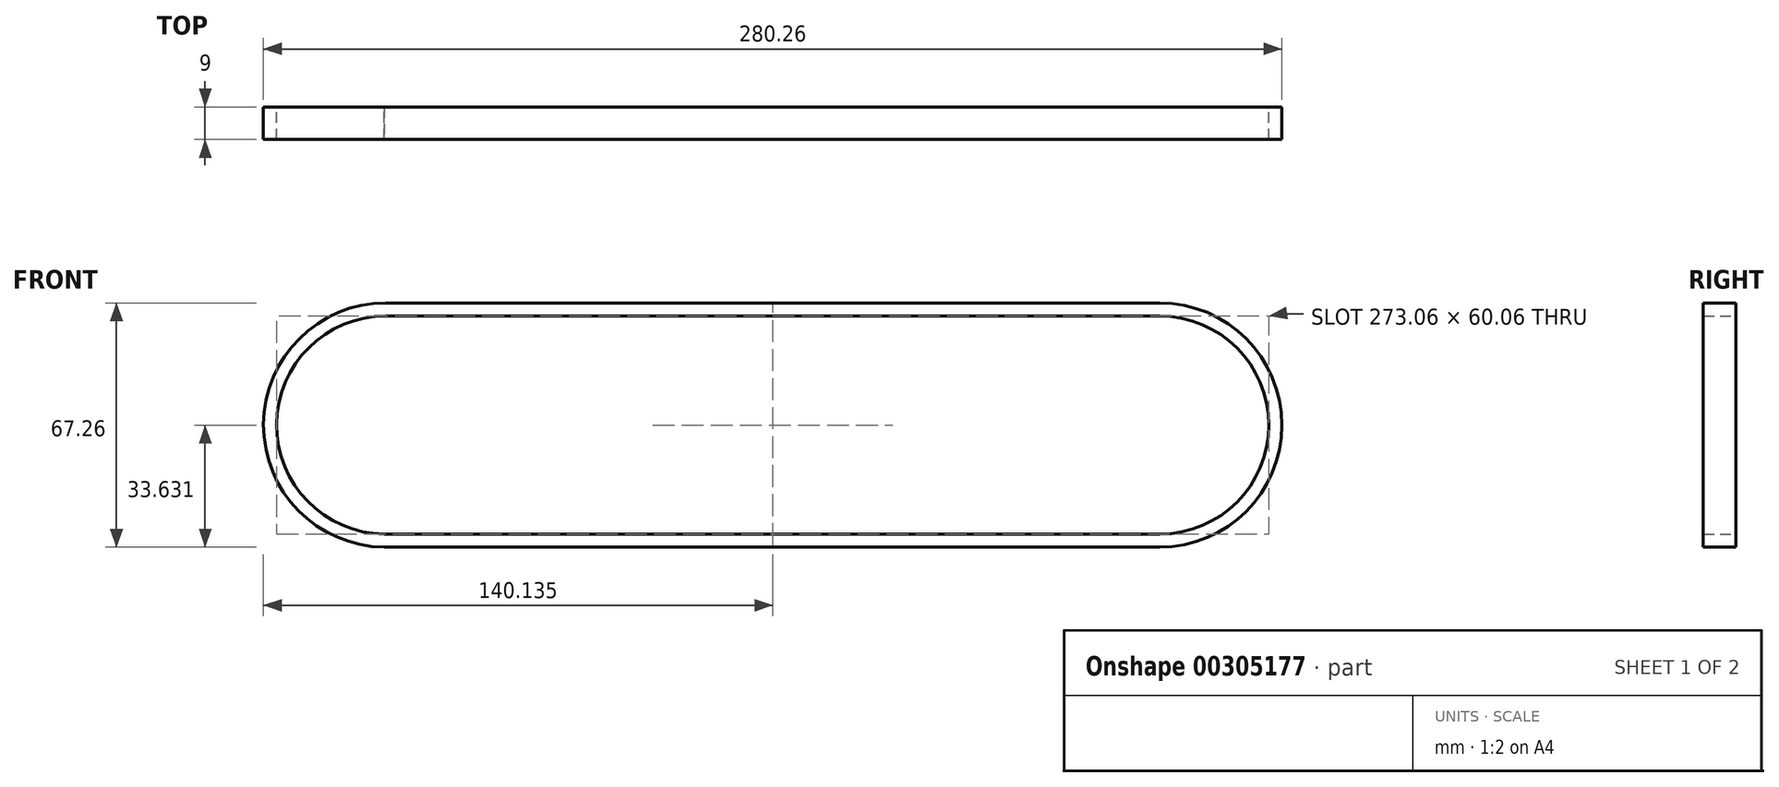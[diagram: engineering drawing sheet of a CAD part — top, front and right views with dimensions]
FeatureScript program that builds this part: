
annotation { "Feature Type Name" : "Feature", "Feature Type Description" : "" }
export const myFeature = defineFeature(function(context is Context, id is Id, definition is map)
    precondition{}
    {
        {
            var Q0;
            Q0=qCreatedBy(makeId("Front.planeOp"),FACE);
            var sketch = newSketch(context, id + "F0", { "sketchPlane" : qUnion([Q0])});
            skLineSegment(sketch, "E0.left", {"start": v(-525.03, 486.56) * mm, "end": v(-525.03, 486.56) * mm});
            skLineSegment(sketch, "E1", {"start": v(64.33, 486.56) * mm, "end": v(64.33, 701.79) * mm, "construction": true});
            skLineSegment(sketch, "E2", {"start": v(-522.39, 458.03) * mm, "end": v(12.71, 507.63) * mm});
            skArc(sketch, "E3", {"start": v(12.71, 507.63) * mm, "mid": v(4.8, 475.52) * mm, "end": v(30.9, 495.85) * mm});
            skArc(sketch, "E4", {"start": v(30.9, 495.85) * mm, "mid": v(23.84, 504.9) * mm, "end": v(12.71, 507.63) * mm});
            skArc(sketch, "E5", {"start": v(97.76, 477.26) * mm, "mid": v(104.86, 468.18) * mm, "end": v(116.06, 465.49) * mm});
            skArc(sketch, "E6", {"start": v(116.06, 465.49) * mm, "mid": v(123.8, 497.62) * mm, "end": v(97.76, 477.26) * mm});
            skArc(sketch, "E7", {"start": v(-525.12, 515.2) * mm, "mid": v(-553.65, 485.2) * mm, "end": v(-522.39, 458.03) * mm});
            skArc(sketch, "E8", {"start": v(-522.39, 458.03) * mm, "mid": v(-496.41, 487.93) * mm, "end": v(-525.12, 515.2) * mm});
            skLineSegment(sketch, "E9", {"start": v(-525.03, 486.56) * mm, "end": v(652.97, 490.2) * mm, "construction": true});
            skPoint(sketch, "E10.startSnap0", {"position": v(104.86, 468.18) * mm});
            skLineSegment(sketch, "E11", {"start": v(64.78, 463.39) * mm, "end": v(653.05, 465.2) * mm});
            skLineSegment(sketch, "E12", {"start": v(652.78, 515.2) * mm, "end": v(116.06, 465.49) * mm});
            skLineSegment(sketch, "E13", {"start": v(64.33, 513.38) * mm, "end": v(-525.12, 515.2) * mm});
            skLineSegment(sketch, "E14", {"start": v(30.9, 495.85) * mm, "end": v(42.8, 475.68) * mm});
            skLineSegment(sketch, "E15", {"start": v(97.76, 477.26) * mm, "end": v(86.72, 499.5) * mm});
            skArc(sketch, "E16", {"start": v(64.33, 513.38) * mm, "mid": v(42.62, 500.78) * mm, "end": v(42.8, 475.68) * mm});
            skArc(sketch, "E17", {"start": v(86.72, 499.5) * mm, "mid": v(77.5, 509.63) * mm, "end": v(64.33, 513.38) * mm});
            skArc(sketch, "E18", {"start": v(652.78, 515.2) * mm, "mid": v(627.97, 490.07) * mm, "end": v(653.05, 465.2) * mm});
            skArc(sketch, "E19", {"start": v(653.05, 465.2) * mm, "mid": v(677.97, 490.34) * mm, "end": v(652.78, 515.2) * mm});
            skArc(sketch, "E20", {"start": v(42.8, 475.68) * mm, "mid": v(52.13, 466.56) * mm, "end": v(64.78, 463.39) * mm});
            skArc(sketch, "E21", {"start": v(64.78, 463.39) * mm, "mid": v(85.7, 475.4) * mm, "end": v(86.72, 499.5) * mm});
            skLineSegment(sketch, "E22", {"start": v(-525.03, 262.8) * mm, "end": v(652.97, 262.8) * mm, "construction": true});
            skLineSegment(sketch, "E23", {"start": v(63.97, 262.8) * mm, "end": v(63.97, 388.17) * mm, "construction": true});
            skLineSegment(sketch, "E24", {"start": v(-525.03, 230.98) * mm, "end": v(1.52, 285.15) * mm});
            skLineSegment(sketch, "E25", {"start": v(-525.03, 294.64) * mm, "end": v(63.97, 294.64) * mm});
            skLineSegment(sketch, "E26", {"start": v(19.1, 276.61) * mm, "end": v(36.47, 246.79) * mm});
            skLineSegment(sketch, "E27", {"start": v(63.97, 230.98) * mm, "end": v(652.97, 230.98) * mm});
            skLineSegment(sketch, "E28", {"start": v(91.47, 278.83) * mm, "end": v(108.85, 249) * mm});
            skLineSegment(sketch, "E29", {"start": v(125.77, 240.4) * mm, "end": v(649.7, 294.47) * mm});
            skArc(sketch, "E30", {"start": v(-525.03, 294.64) * mm, "mid": v(-556.86, 262.8) * mm, "end": v(-525.03, 230.98) * mm});
            skArc(sketch, "E31", {"start": v(-525.03, 230.98) * mm, "mid": v(-493.2, 262.8) * mm, "end": v(-525.03, 294.64) * mm});
            skArc(sketch, "E32", {"start": v(1.36, 285.1) * mm, "mid": v(-3.59, 252.02) * mm, "end": v(19.1, 276.61) * mm});
            skArc(sketch, "E33", {"start": v(19.1, 276.61) * mm, "mid": v(11.53, 283.59) * mm, "end": v(1.36, 285.1) * mm});
            skArc(sketch, "E34", {"start": v(36.47, 246.79) * mm, "mid": v(48.1, 235.21) * mm, "end": v(63.97, 230.98) * mm});
            skArc(sketch, "E35", {"start": v(63.97, 230.98) * mm, "mid": v(91.57, 246.94) * mm, "end": v(91.47, 278.83) * mm});
            skArc(sketch, "E36", {"start": v(63.97, 294.64) * mm, "mid": v(36.37, 278.67) * mm, "end": v(36.47, 246.79) * mm});
            skArc(sketch, "E37", {"start": v(91.47, 278.83) * mm, "mid": v(79.83, 290.4) * mm, "end": v(63.97, 294.64) * mm});
            skArc(sketch, "E38", {"start": v(108.85, 249) * mm, "mid": v(116.04, 242.2) * mm, "end": v(125.77, 240.4) * mm});
            skArc(sketch, "E39", {"start": v(125.77, 240.4) * mm, "mid": v(131.9, 273.4) * mm, "end": v(108.85, 249) * mm});
            skArc(sketch, "E40", {"start": v(649.7, 294.47) * mm, "mid": v(621.18, 261.17) * mm, "end": v(652.97, 230.98) * mm});
            skArc(sketch, "E41", {"start": v(652.97, 230.98) * mm, "mid": v(684.76, 264.44) * mm, "end": v(649.7, 294.47) * mm});
            skCircle(sketch, "E42", {"center": v(652.97, 2.27) * mm, "radius": 31.83 * mm});
            skLineSegment(sketch, "E43", {"start": v(5.35, -6.02) * mm, "end": v(43.27, 26.45) * mm});
            skLineSegment(sketch, "E44", {"start": v(-7.53, -10.16) * mm, "end": v(-522.3, 33.99) * mm});
            skArc(sketch, "E45", {"start": v(-522.3, 33.99) * mm, "mid": v(-556.83, 3.63) * mm, "end": v(-525.03, -29.56) * mm});
            skArc(sketch, "E46", {"start": v(-525.03, -29.56) * mm, "mid": v(-517.68, -28.7) * mm, "end": v(-510.72, -26.16) * mm});
            skArc(sketch, "E47", {"start": v(-7.53, -10.16) * mm, "mid": v(-0.67, -9.39) * mm, "end": v(5.35, -6.02) * mm});
            skArc(sketch, "E48", {"start": v(5.35, -6.02) * mm, "mid": v(-11.4, 23.93) * mm, "end": v(-7.53, -10.16) * mm});
            skArc(sketch, "E49", {"start": v(43.84, 26.93) * mm, "mid": v(33.99, -8.41) * mm, "end": v(63.97, -29.56) * mm});
            skLineSegment(sketch, "E50", {"start": v(63.97, -29.56) * mm, "end": v(63.97, -29.56) * mm});
            skLineSegment(sketch, "E51", {"start": v(-525.03, 2.27) * mm, "end": v(170.78, 2.27) * mm, "construction": true});
            skLineSegment(sketch, "E52", {"start": v(-525.03, 2.27) * mm, "end": v(-525.03, 58.63) * mm, "construction": true});
            skLineSegment(sketch, "E53", {"start": v(63.97, -29.56) * mm, "end": v(-453.54, 14.7) * mm});
            skArc(sketch, "E54", {"start": v(-462.9, 12.9) * mm, "mid": v(-451.72, -19.91) * mm, "end": v(-453.54, 14.7) * mm});
            skArc(sketch, "E55", {"start": v(-453.54, 14.7) * mm, "mid": v(-458.34, 14.46) * mm, "end": v(-462.9, 12.9) * mm});
            skLineSegment(sketch, "E56", {"start": v(-525.03, -29.56) * mm, "end": v(-525.03, -29.56) * mm});
            skArc(sketch, "E57", {"start": v(-510.72, -26.16) * mm, "mid": v(-493.77, 8.3) * mm, "end": v(-522.3, 33.99) * mm});
            skArc(sketch, "E58", {"start": v(43.27, 26.45) * mm, "mid": v(84.39, -22.15) * mm, "end": v(43.84, 26.93) * mm});
            skArc(sketch, "E59", {"start": v(63.97, -29.56) * mm, "mid": v(93.83, 13.3) * mm, "end": v(43.27, 26.45) * mm});
            skLineSegment(sketch, "E60", {"start": v(-504.33, -21.9) * mm, "end": v(-466.41, 10.56) * mm});
            skLineSegment(sketch, "E61", {"start": v(-504.33, -244.07) * mm, "end": v(154.7, -244.07) * mm, "construction": true});
            skLineSegment(sketch, "E62", {"start": v(60.46, -282.1) * mm, "end": v(-432.72, -236.64) * mm});
            skLineSegment(sketch, "E63", {"start": v(-446.45, -241.44) * mm, "end": v(-446.6, -241.6) * mm});
            skLineSegment(sketch, "E64", {"start": v(-500.82, -206.03) * mm, "end": v(-7.64, -251.5) * mm});
            skLineSegment(sketch, "E65", {"start": v(6.1, -246.69) * mm, "end": v(37.5, -216.51) * mm});
            skArc(sketch, "E66", {"start": v(37.5, -216.51) * mm, "mid": v(27.91, -256.68) * mm, "end": v(60.46, -282.1) * mm});
            skArc(sketch, "E67", {"start": v(60.46, -282.1) * mm, "mid": v(100.03, -231.45) * mm, "end": v(37.5, -216.51) * mm});
            skArc(sketch, "E68", {"start": v(6.1, -246.69) * mm, "mid": v(-11.81, -217.55) * mm, "end": v(-7.64, -251.5) * mm});
            skArc(sketch, "E69", {"start": v(-7.64, -251.5) * mm, "mid": v(-0.25, -250.58) * mm, "end": v(6.1, -246.69) * mm});
            skLineSegment(sketch, "E70", {"start": v(-446.6, -241.6) * mm, "end": v(-477.87, -271.62) * mm});
            skArc(sketch, "E71", {"start": v(-446.45, -241.44) * mm, "mid": v(-428.55, -270.58) * mm, "end": v(-432.72, -236.64) * mm});
            skArc(sketch, "E72", {"start": v(-432.72, -236.64) * mm, "mid": v(-440.1, -237.55) * mm, "end": v(-446.45, -241.44) * mm});
            skArc(sketch, "E73", {"start": v(-477.87, -271.62) * mm, "mid": v(-468.27, -231.45) * mm, "end": v(-500.82, -206.03) * mm});
            skArc(sketch, "E74", {"start": v(-500.82, -206.03) * mm, "mid": v(-540.38, -256.68) * mm, "end": v(-477.87, -271.62) * mm});
            skLineSegment(sketch, "E75", {"start": v(-504.33, -545.9) * mm, "end": v(460.67, -545.9) * mm, "construction": true});
            skPoint(sketch, "E76.centerSnap0", {"position": v(-21.83, -545.9) * mm});
            skLineSegment(sketch, "E77", {"start": v(-504.33, -514.08) * mm, "end": v(460.67, -514.08) * mm});
            skLineSegment(sketch, "E78", {"start": v(460.28, -577.74) * mm, "end": v(-383.7, -544.92) * mm});
            skLineSegment(sketch, "E79", {"start": v(-495.46, -576.48) * mm, "end": v(-388.78, -545.54) * mm});
            skArc(sketch, "E80", {"start": v(-388.78, -545.54) * mm, "mid": v(-382.38, -576.8) * mm, "end": v(-383.7, -544.92) * mm});
            skArc(sketch, "E81", {"start": v(-383.7, -544.92) * mm, "mid": v(-386.27, -545.03) * mm, "end": v(-388.78, -545.54) * mm});
            skArc(sketch, "E82", {"start": v(-495.46, -576.48) * mm, "mid": v(-472.81, -541.43) * mm, "end": v(-504.33, -514.08) * mm});
            skArc(sketch, "E83", {"start": v(-504.33, -514.08) * mm, "mid": v(-535.84, -550.39) * mm, "end": v(-495.46, -576.48) * mm});
            skArc(sketch, "E84", {"start": v(460.28, -577.74) * mm, "mid": v(492.5, -546.1) * mm, "end": v(460.67, -514.08) * mm});
            skArc(sketch, "E85", {"start": v(460.67, -514.08) * mm, "mid": v(428.85, -545.7) * mm, "end": v(460.28, -577.74) * mm});
            skLineSegment(sketch, "E86", {"start": v(460.67, -514.08) * mm, "end": v(673.67, -514.08) * mm});
            skLineSegment(sketch, "E87", {"start": v(460.28, -577.74) * mm, "end": v(673.67, -577.74) * mm});
            skArc(sketch, "E88", {"start": v(673.67, -577.74) * mm, "mid": v(705.5, -545.9) * mm, "end": v(673.67, -514.08) * mm});
            skSolve(sketch);
        }
        {
            var Q0;
            Q0=sQuery(id+"F0.wireOp",EDGE,"E86");
            cPlane(context, id + "F1", {"entities" : qUnion([Q0]), "cplaneType" : CPlaneType.MID_PLANE, "offset" : 25 * mm, "width" : 150 * mm, "height" : 150 * mm});
        }
        {
            var Q0;
            Q0=qCreatedBy(id+"F1.planeOp",FACE);
            var sketch = newSketch(context, id + "F2", { "sketchPlane" : qUnion([Q0])});
            skPoint(sketch, "E89.0", {"position": v(0, -514.08) * mm});
            skLineSegment(sketch, "E90.bottom", {"start": v(-4.5, -512.28) * mm, "end": v(4.5, -512.28) * mm});
            skLineSegment(sketch, "E90.top", {"start": v(-4.5, -515.88) * mm, "end": v(4.5, -515.88) * mm});
            skLineSegment(sketch, "E90.left", {"start": v(-4.5, -512.28) * mm, "end": v(-4.5, -515.88) * mm});
            skLineSegment(sketch, "E90.right", {"start": v(4.5, -512.28) * mm, "end": v(4.5, -515.88) * mm});
            skSolve(sketch);
        }
        {
            var Q0;
            Q0=makeQuery(id+"F2.imprint","IMPRINT",FACE,{"disambiguationData":[TD([[makeQuery(id+"F2.imprint","IMPRINT",EDGE,{"derivedFrom":sQuery(id+"F2.wireOp",EDGE,"E90.bottom")}),-1.0]])]});
            var Q1;
            Q1=sQuery(id+"F0.wireOp",EDGE,"E86");
            var Q2;
            Q2=sQuery(id+"F0.wireOp",EDGE,"E85");
            var Q3;
            Q3=sQuery(id+"F0.wireOp",EDGE,"E87");
            var Q4;
            Q4=sQuery(id+"F0.wireOp",EDGE,"E88");
            sweep(context, id + "F3", {"profiles" : qUnion([Q0]), "path" : qUnion([Q1, Q2, Q3, Q4])});
        }
    });
